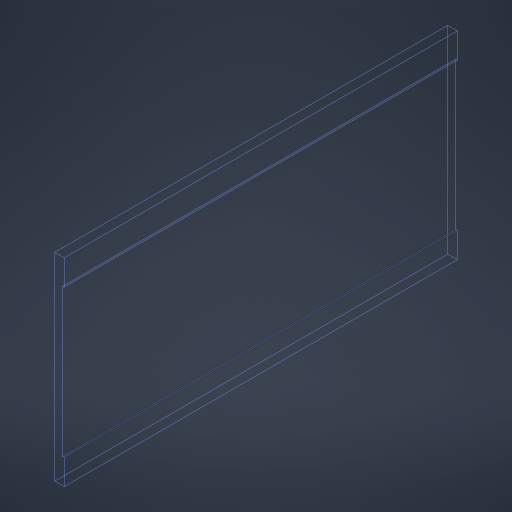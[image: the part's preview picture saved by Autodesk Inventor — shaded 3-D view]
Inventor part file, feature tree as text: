
AUTODESK INVENTOR PART (.ipt)
format: ipt  version: 2024 (Build 280153000, 153)  size: 206,336 bytes
history: native  units: mm
features: extrude x2, sketch x2
ambient origin geometry x8: Origin, YZ Plane, XZ Plane, XY Plane, X Axis, Y Axis, Z Axis, Center Point
bodies: Solid1 (feature_tree)
feature tree (4):
  extrude  "Extrusion1"  Depth=496.0mm
  extrude  "Extrusion3"  Depth=32.0mm
  sketch  "Sketch1"  dims[d0=10.0mm d1=496.0mm]
  sketch  "Sketch2"  dims[d2=250.0mm d3=0.0mm d4=32.0mm d5=32.0mm d6=186.0mm d9=2.0mm d10=0.0mm]
